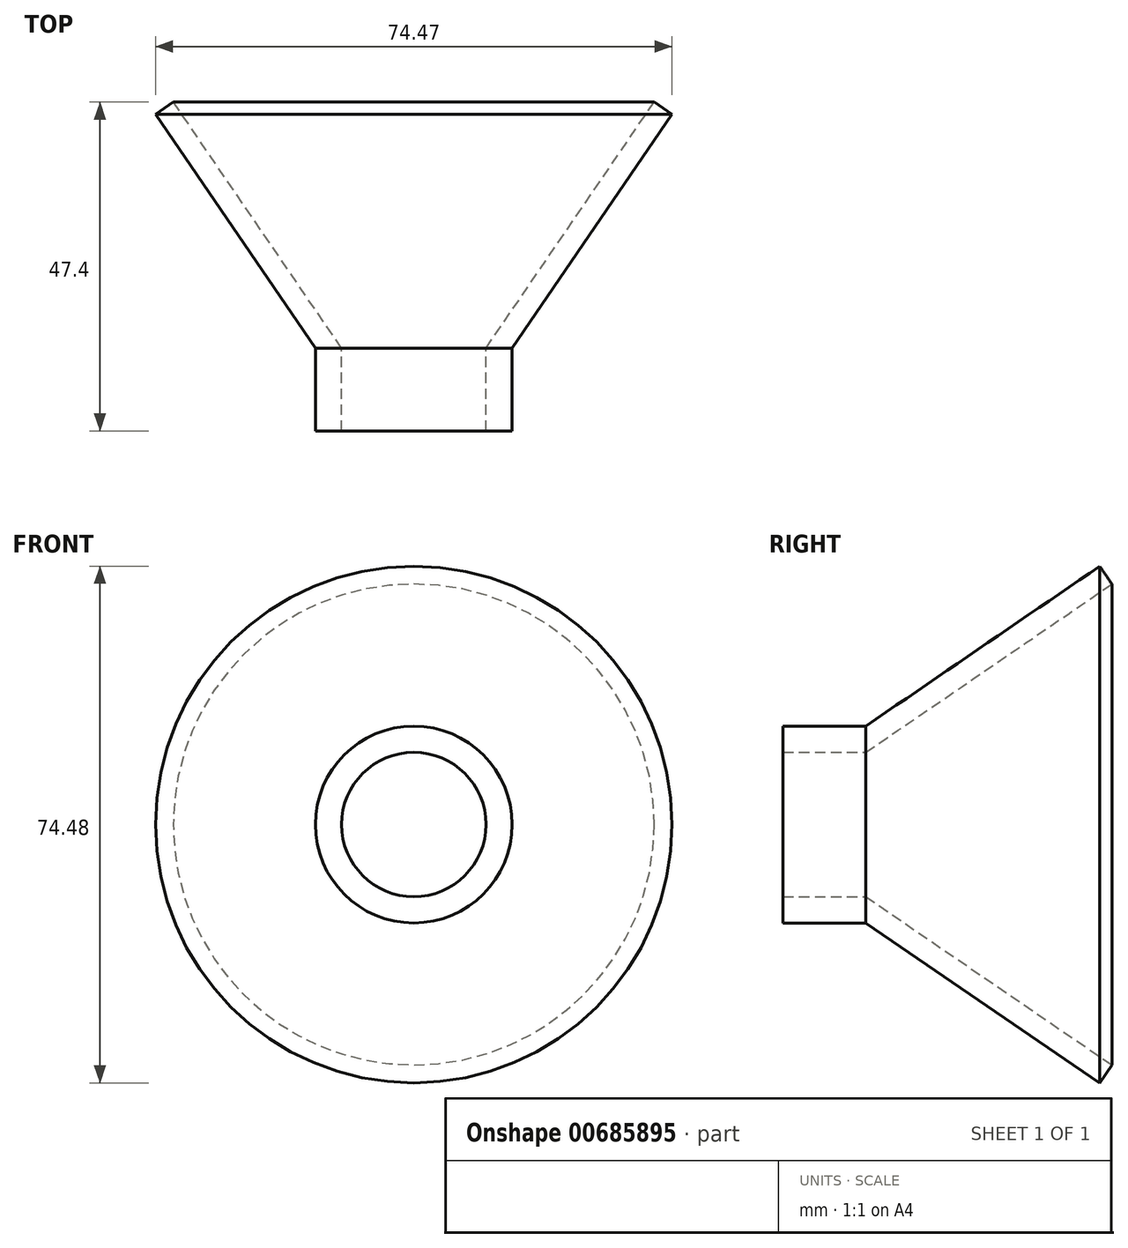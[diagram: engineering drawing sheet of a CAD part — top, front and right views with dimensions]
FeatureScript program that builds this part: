
annotation { "Feature Type Name" : "Feature", "Feature Type Description" : "" }
export const myFeature = defineFeature(function(context is Context, id is Id, definition is map)
    precondition{}
    {
        {
            var Q0;
            Q0=qCreatedBy(makeId("Top.planeOp"),FACE);
            var sketch = newSketch(context, id + "F0", { "sketchPlane" : qUnion([Q0])});
            skLineSegment(sketch, "E0", {"start": v(0, 0) * mm, "end": v(0, -11.93) * mm});
            skLineSegment(sketch, "E1", {"start": v(0, 0) * mm, "end": v(24.25, 35.47) * mm});
            skLineSegment(sketch, "E2", {"start": v(24.25, 35.47) * mm, "end": v(26.83, 33.7) * mm});
            skLineSegment(sketch, "E3", {"start": v(26.83, 33.7) * mm, "end": v(3.78, 0) * mm});
            skLineSegment(sketch, "E4", {"start": v(3.78, 0) * mm, "end": v(3.78, -11.93) * mm});
            skLineSegment(sketch, "E5", {"start": v(3.78, -11.93) * mm, "end": v(0, -11.93) * mm});
            skLineSegment(sketch, "E6", {"start": v(-10.4, 3.72) * mm, "end": v(-10.4, -11.93) * mm});
            skSolve(sketch);
        }
        {
            var Q0;
            Q0=makeQuery(id+"F0.imprint","IMPRINT",FACE,{"disambiguationData":[TD([[makeQuery(id+"F0.imprint","IMPRINT",EDGE,{"derivedFrom":sQuery(id+"F0.wireOp",EDGE,"E0")}),1.0]])]});
            var Q1;
            Q1=sQuery(id+"F0.wireOp",EDGE,"E6");
            revolve(context, id + "F1", {"entities" : qUnion([Q0]), "axis" : qUnion([Q1]), "revolveType" : RevolveType.FULL});
        }
    });
